# Revit family: Data_Device-Work_Area-Leviton-MOS-Wallplate
name_source: partatom
category: Data Devices
units: mm (PartAtom-declared; Revit-internal decimal feet)

## family parameters
Cut with Voids When Loaded = No
Host = Face
Maintain Annotation Orientation = Yes
OmniClass Number = 23.85.50.21
OmniClass Title = Cable Transmission and Reception Equipment
Part Type = Normal
Room Calculation Point = No
Round Connector Dimension = Use Diameter
Shared = Yes

## types (2) — shared parameters
Annotation Symbol is Visible = Yes
Assembly Code = D5030600
Check for Latest Version = http://www.leviton.com
Date Last Modified = March 3, 2014
Default Elevation = 18 "
Equipment Abbreviation = MOS
Family Version = 1.0.3
Manufacturer = Leviton
Model Disclaimer = http://www.leviton.com
Product Documentation Link = http://www.leviton.com
Provide Feedback = http://www.leviton.com
URL = http://www.leviton.com
z Collapse = Yes
z Depth = 0.25 "
z Height = 2.9 "
zero-valued in all types: Minimum Order Quantity, Quantity per Package, z Distance

## per-type parameters (varying)
| type | Description | Part Description | z Is Dual Gang | z Is Single Gang | z Leviton Type | z Width |
| Single Gang | MOS Wallplate, Single Gang | MOS Wallplate, Single Gang | No | Yes | 1 | 1.86 " |
| Dual Gang | MOS Wallplate, Dual Gang | MOS Wallplate, Dual Gang | Yes | No | 2 | 3.75 " |

## geometry (parser evidence)
native form markers: Blend x42, Sweep x5
no freeform markers — native parametric forms only
